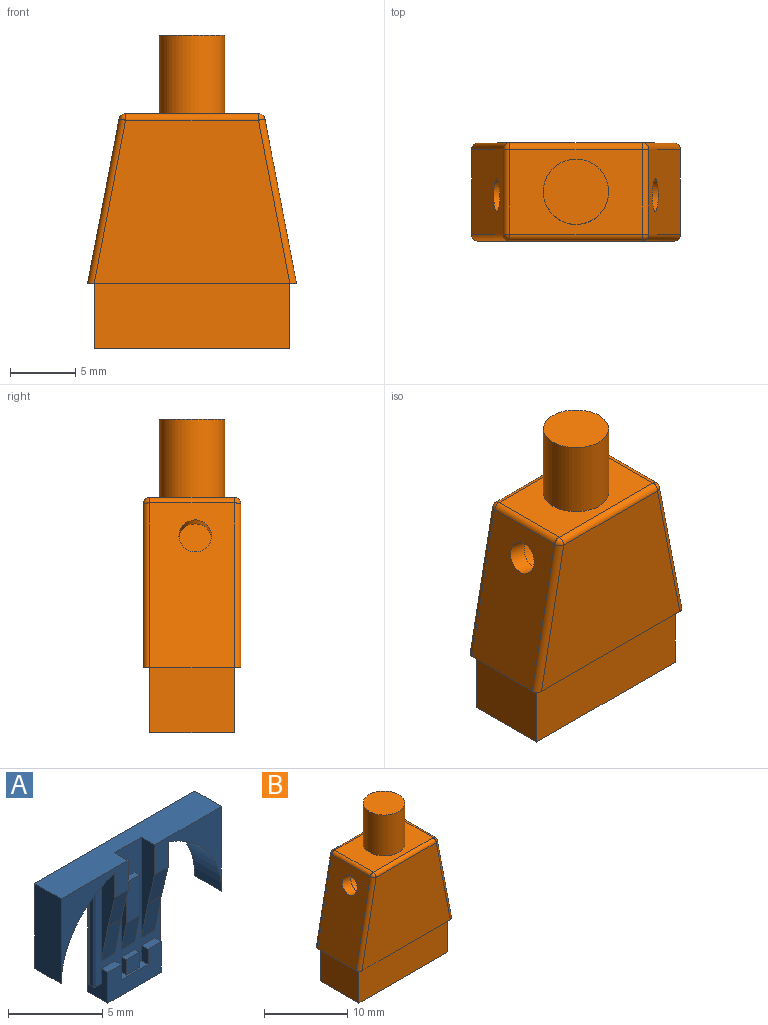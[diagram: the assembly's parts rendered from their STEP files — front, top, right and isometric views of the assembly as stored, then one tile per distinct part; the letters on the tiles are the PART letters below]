
ASSEMBLY  parts=2 mates=1
PART A: 45 faces, bbox 12x2x9 mm
  f0: plane 6.21x1mm, normal (1,0,0), area 3.8mm2, adj f11,f14,f16,f18,f31
  f1: plane 8.69x1.5mm, normal (-1,0,0), area 5.8mm2, adj f5,f7,f15,f17,f18,f33,f35,f37
  f2: plane 6.21x1mm, normal (-1,0,0), area 3.8mm2, adj f4,f10,f12,f18,f33
  f3: plane 8.69x1.5mm, normal (1,0,0), area 5.8mm2, adj f5,f8,f15,f17,f18,f31,f39,f40
  f4: plane 5.5x5mm, normal (0,-1,0), area 8.8mm2, adj f2,f12,f13,f26,f33,f34
  f5: plane 4x2mm, normal (0,-1,0), area 6mm2, adj f1,f3,f7,f8,f15,f21,f27,f29
  f6: plane 1x0.38mm, normal (0,0.06,1), area 0.4mm2, adj f18,f22,f28,f30
  f7: plane 1x0.5mm, normal (0,0.06,1), area 0.5mm2, adj f1,f5,f18,f29
  f8: plane 1x0.5mm, normal (0,0.06,1), area 0.5mm2, adj f3,f5,f18,f27
  f9: plane 1.88x1mm, normal (0,-0.98,-0.2), area 1.9mm2, adj f18,f20,f24,f25
  f10: plane 2.5x1mm, normal (0,-0.98,-0.2), area 2.5mm2, adj f2,f12,f18,f26
  f11: plane 2.5x1mm, normal (0,-0.98,-0.2), area 2.5mm2, adj f0,f14,f18,f23
  f12: plane 2.09x1mm, normal (0,-0.97,-0.23), area 2.1mm2, adj f2,f4,f10,f26
  f13: plane 12x2mm, normal (0,0,1), area 22mm2, adj f4,f16,f17,f18,f23,f26,f32,f34
  f14: plane 2.09x1mm, normal (0,-0.97,-0.23), area 2.1mm2, adj f0,f11,f16,f23
  f15: plane 4x1.5mm, normal (0,0,-1), area 6mm2, adj f1,f3,f5,f17
  f16: plane 5.5x5mm, normal (0,-1,0), area 8.8mm2, adj f0,f13,f14,f23,f31,f32
  f17: plane 12x9mm, normal (0,1,0), area 49.7mm2, adj f1,f3,f13,f15,f31,f32,f33,f34
  f18: plane 8x4.8mm, normal (0,-1,0), area 17.6mm2, adj f0,f1,f2,f3,f6,f7,f8,f9
  f19: plane 1x0.38mm, normal (0,0,1), area 0.4mm2, adj f18,f20,f24,f25
  f20: plane 2.65x1mm, normal (0,-1,0), area 2.7mm2, adj f9,f19,f24,f25
  f21: plane 2x0.5mm, normal (0,0,1), area 0.6mm2, adj f5,f18,f22,f27,f28,f29,f30
  f22: plane 1x0.99mm, normal (0,-1,0), area 1mm2, adj f6,f21,f28,f30
  f23: plane 6.53x1mm, normal (-1,0,0), area 4.1mm2, adj f11,f13,f14,f16,f18
  f24: plane 4.53x0.38mm, normal (1,0,0), area 1.3mm2, adj f9,f18,f19,f20
  f25: plane 4.53x0.38mm, normal (-1,0,0), area 1.3mm2, adj f9,f18,f19,f20
  f26: plane 6.53x1mm, normal (1,0,0), area 4.1mm2, adj f4,f10,f12,f13,f18
  f27: plane 1x0.5mm, normal (-1,0,0), area 0.5mm2, adj f5,f8,f18,f21
  f28: plane 0.99x0.38mm, normal (1,0,0), area 0.4mm2, adj f6,f18,f21,f22
  f29: plane 1x0.5mm, normal (1,0,0), area 0.5mm2, adj f5,f7,f18,f21
  f30: plane 0.99x0.38mm, normal (-1,0,0), area 0.4mm2, adj f6,f18,f21,f22
  f31: extruded ~5.19x4mm, area 13.7mm2, adj f0,f3,f16,f17,f18,f32,f38,f39
  f32: plane 5.5x2mm, normal (1,0,0), area 11mm2, adj f13,f16,f17,f31
  f33: extruded ~5.19x4mm, area 13.7mm2, adj f1,f2,f4,f17,f18,f34,f35,f36
  f34: plane 5.5x2mm, normal (-1,0,0), area 11mm2, adj f4,f13,f17,f33
  f35: plane 7.69x0.4mm, normal (0,1,0), area 3mm2, adj f1,f33,f37,f44
  f36: plane 7.5x0.3mm, normal (-1,0,0), area 2.2mm2, adj f33,f37,f43,f44
  f37: plane 0.5x0.5mm, normal (0,0,-1), area 0.2mm2, adj f1,f18,f35,f36,f43,f44
  f38: plane 7.5x0.3mm, normal (1,0,0), area 2.2mm2, adj f31,f40,f41,f42
  f39: plane 7.69x0.4mm, normal (0,1,0), area 3mm2, adj f3,f31,f40,f42
  f40: plane 0.5x0.5mm, normal (0,0,-1), area 0.2mm2, adj f3,f18,f38,f39,f41,f42
  f41: cylinder r=0.1mm len=7.54mm, axis (0,0,-1), area 1.2mm2, adj f18,f31,f38,f40
  f42: cylinder r=0.1mm len=7.54mm, axis (0,0,-1), area 1.2mm2, adj f31,f38,f39,f40
  f43: cylinder r=0.1mm len=7.54mm, axis (0,0,-1), area 1.2mm2, adj f18,f33,f36,f37
  f44: cylinder r=0.1mm len=7.54mm, axis (0,0,1), area 1.2mm2, adj f33,f35,f36,f37
PART B: 57 faces, bbox 16x7.5x24 mm
  f0: plane 16x7.5mm, normal (0,0,-1), area 22.4mm2, adj f1,f2,f4,f5,f8,f10,f13,f16
  f1: plane 12.59x6.5mm, normal (-0.98,0,0.19), area 78.5mm2, adj f0,f8,f9,f10,f20
  f2: plane 12.59x6.5mm, normal (0.98,0,0.19), area 78.5mm2, adj f0,f13,f16,f19,f21
  f3: plane 10.17x6.5mm, normal (0,0,1), area 46.5mm2, adj f6,f9,f14,f15,f19
  f4: plane 14.98x12.5mm, normal (0,-1,0), area 157.2mm2, adj f0,f8,f13,f14
  f5: plane 14.98x12.5mm, normal (0,1,0), area 157.2mm2, adj f0,f10,f15,f16
  f6: cylinder r=2.5mm len=6mm, axis (0,0,-1), area 94.2mm2, adj f3,f7
  f7: plane 5x5mm, normal (0,0,1), area 19.6mm2, adj f6
  f8: cylinder r=0.5mm len=12.69mm, axis (0.19,0,0.98), area 10mm2, adj f0,f1,f4,f11
  f9: cylinder r=0.5mm len=6.5mm, axis (0,1,0), area 4.5mm2, adj f1,f3,f11,f12
  f10: cylinder r=0.5mm len=12.69mm, axis (-0.19,0,-0.98), area 10mm2, adj f0,f1,f5,f12
  f11: sphere r=0.5mm, area 0.3mm2, adj f8,f9,f14
  f12: sphere r=0.5mm, area 0.3mm2, adj f9,f10,f15
  f13: cylinder r=0.5mm len=12.69mm, axis (0.19,0,-0.98), area 10mm2, adj f0,f2,f4,f17
  f14: cylinder r=0.5mm len=10.17mm, axis (1,0,0), area 8mm2, adj f3,f4,f11,f17
  f15: cylinder r=0.5mm len=10.17mm, axis (-1,0,0), area 8mm2, adj f3,f5,f12,f18
  f16: cylinder r=0.5mm len=12.69mm, axis (-0.19,0,0.98), area 10mm2, adj f0,f2,f5,f18
  f17: sphere r=0.5mm, area 0.3mm2, adj f13,f14,f19
  f18: sphere r=0.5mm, area 0.3mm2, adj f15,f16,f19
  f19: cylinder r=0.5mm len=6.5mm, axis (0,1,0), area 4.5mm2, adj f2,f3,f17,f18
  f20: cylinder r=1.25mm len=2.74mm, axis (-0.98,0,0.19), area 11.8mm2, adj f1,f24
  f21: cylinder r=1.25mm len=2.74mm, axis (0.98,0,0.19), area 11.8mm2, adj f2,f27
  f22: cylinder r=2mm len=4.68mm, axis (-0.98,0,0.19), area 50.3mm2, adj f23,f24
  f23: plane 4x3.93mm, normal (-0.98,0,0.19), area 12.6mm2, adj f22
  f24: plane 4x3.93mm, normal (0.98,0,-0.19), area 7.7mm2, adj f20,f22
  f25: cylinder r=2mm len=4.68mm, axis (0.98,0,0.19), area 50.3mm2, adj f26,f27
  f26: plane 4x3.93mm, normal (0.98,0,0.19), area 12.6mm2, adj f25
  f27: plane 4x3.93mm, normal (-0.98,0,-0.19), area 7.7mm2, adj f21,f25
  f28: plane 14.98x5mm, normal (0,-1,0), area 74.9mm2, adj f0,f29,f33,f34
  f29: plane 6.5x5mm, normal (-1,0,0), area 32.5mm2, adj f0,f28,f30,f34
  f30: plane 14.98x5mm, normal (0,1,0), area 74.9mm2, adj f0,f29,f33,f34
  f31: plane 5.5x5mm, normal (1,0,0), area 27.5mm2, adj f34,f51,f53,f54
  f32: plane 5.5x5mm, normal (-1,0,0), area 27.5mm2, adj f34,f53,f54,f56
  f33: plane 6.5x5mm, normal (1,0,0), area 32.5mm2, adj f0,f28,f30,f34
  f34: plane 14.98x6.5mm, normal (0,0,-1), area 20.6mm2, adj f28,f29,f30,f31,f32,f33,f53,f54
  f35: plane 2x2mm, normal (1,0,0), area 4mm2, adj f38,f39,f40,f41
  f36: plane 2x2mm, normal (-1,0,0), area 4mm2, adj f42,f43,f44,f45
  f37: plane 3x2mm, normal (0,-1,0), area 6mm2, adj f46,f47,f48,f49
  f38: plane 2x0.5mm, normal (0,0,1), area 1mm2, adj f35,f39,f41,f52
  f39: plane 2x0.5mm, normal (0,-1,0), area 1mm2, adj f35,f38,f40,f52
  f40: plane 2x0.5mm, normal (0,0,-1), area 1mm2, adj f35,f39,f41,f52
  f41: plane 2x0.5mm, normal (0,1,0), area 1mm2, adj f35,f38,f40,f52
  f42: plane 2x0.5mm, normal (0,-1,0), area 1mm2, adj f36,f43,f45,f55
  f43: plane 2x0.5mm, normal (0,0,1), area 1mm2, adj f36,f42,f44,f55
  f44: plane 2x0.5mm, normal (0,1,0), area 1mm2, adj f36,f43,f45,f55
  f45: plane 2x0.5mm, normal (0,0,-1), area 1mm2, adj f36,f42,f44,f55
  f46: plane 2x0.5mm, normal (1,0,0), area 1mm2, adj f37,f47,f49,f53
  f47: plane 3x0.5mm, normal (0,0,1), area 1.5mm2, adj f37,f46,f48,f53
  f48: plane 2x0.5mm, normal (-1,0,0), area 1mm2, adj f37,f47,f49,f53
  f49: plane 3x0.5mm, normal (0,0,-1), area 1.5mm2, adj f37,f46,f48,f53
  f50: plane 12.5x5.5mm, normal (0,0,-1), area 68.8mm2, adj f52,f53,f54,f55
  f51: plane 5.5x0.73mm, normal (0,0,-1), area 4mm2, adj f31,f52,f53,f54
  f52: plane 6.5x5.5mm, normal (1,0,0), area 31.8mm2, adj f38,f39,f40,f41,f50,f51,f53,f54
  f53: plane 13.96x11.5mm, normal (0,-1,0), area 145.1mm2, adj f31,f32,f34,f46,f47,f48,f49,f50
  f54: plane 13.96x11.5mm, normal (0,1,0), area 151.1mm2, adj f31,f32,f34,f50,f51,f52,f55,f56
  f55: plane 6.5x5.5mm, normal (-1,0,0), area 31.8mm2, adj f42,f43,f44,f45,f50,f53,f54,f56
  f56: plane 5.5x0.73mm, normal (0,0,-1), area 4mm2, adj f32,f53,f54,f55
PLACE A t=(6.75,8.32,-0.09)mm
PLACE B t=(0.75,12.82,-6.59)mm
MATE fastened A.f4 <-> B.f54  axis (0,-1,0) through (7.75,6.32,-0.09)mm
